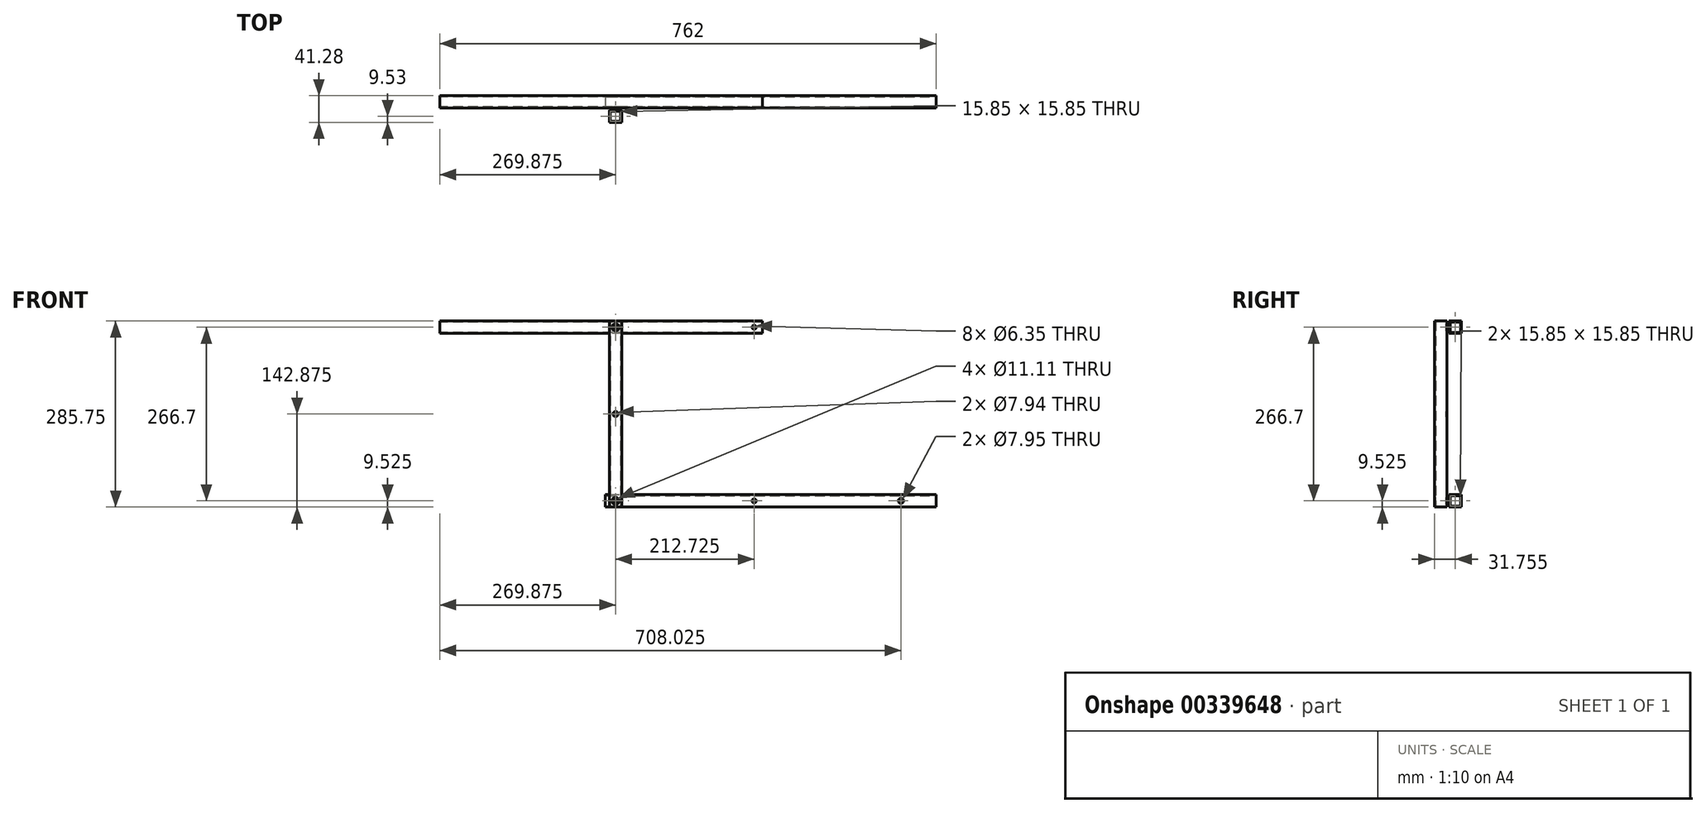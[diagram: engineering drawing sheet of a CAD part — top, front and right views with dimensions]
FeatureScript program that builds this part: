
annotation { "Feature Type Name" : "Feature", "Feature Type Description" : "" }
export const myFeature = defineFeature(function(context is Context, id is Id, definition is map)
    precondition{}
    {
        {
            var Q0;
            Q0=qCreatedBy(makeId("Front.planeOp"),FACE);
            var sketch = newSketch(context, id + "F0", { "sketchPlane" : qUnion([Q0])});
            skLineSegment(sketch, "E0.bottom", {"start": v(0, 0) * mm, "end": v(508, 0) * mm});
            skLineSegment(sketch, "E0.top", {"start": v(0, 19.05) * mm, "end": v(508, 19.05) * mm});
            skLineSegment(sketch, "E0.left", {"start": v(0, 0) * mm, "end": v(0, 19.05) * mm});
            skLineSegment(sketch, "E0.right", {"start": v(508, 0) * mm, "end": v(508, 19.05) * mm});
            skSolve(sketch);
        }
        {
            var Q0;
            Q0=makeQuery(id+"F0.imprint","IMPRINT",FACE,{"disambiguationData":[TD([[makeQuery(id+"F0.imprint","IMPRINT",EDGE,{"derivedFrom":sQuery(id+"F0.wireOp",EDGE,"E0.bottom")}),1.0]])]});
            extrude(context, id + "F1", {"entities" : qUnion([Q0]), "oppositeDirection" : true, "depth" : 19.05 * mm});
        }
        {
            var Q0;
            Q0=makeQuery(id+"F1.opExtrude","SWEPT_FACE",FACE,{"disambiguationData":[OSD([sQuery(id+"F0.wireOp",EDGE,"E0.right")])]});
            var Q1;
            Q1=makeQuery(id+"F1.opExtrude","SWEPT_FACE",FACE,{"disambiguationData":[OSD([sQuery(id+"F0.wireOp",EDGE,"E0.left")])]});
            shell(context, id + "F2", {"entities" : qUnion([Q0, Q1]), "thickness" : 1.6 * mm});
        }
        {
            var Q0;
            Q0=makeQuery(id+"F1.opExtrude","CAP_FACE",FACE,{"disambiguationData":[OSD([sQuery(id+"F0.wireOp",EDGE,"E0.bottom"),sQuery(id+"F0.wireOp",EDGE,"E0.top"),sQuery(id+"F0.wireOp",EDGE,"E0.left"),sQuery(id+"F0.wireOp",EDGE,"E0.right")])],"isStart":true});
            var sketch = newSketch(context, id + "F3", { "sketchPlane" : qUnion([Q0])});
            skCircle(sketch, "E1", {"center": v(15.88, 9.53) * mm, "radius": 3.18 * mm});
            skPoint(sketch, "E1.centerSnap0", {"position": v(0, 9.53) * mm});
            skCircle(sketch, "E2", {"center": v(228.6, 9.53) * mm, "radius": 3.18 * mm});
            skSolve(sketch);
        }
        {
            var Q0;
            Q0=makeQuery(id+"F3.imprint","IMPRINT",FACE,{"disambiguationData":[TD([[makeQuery(id+"F3.imprint","IMPRINT",EDGE,{"derivedFrom":sQuery(id+"F3.wireOp",EDGE,"E2")}),1.0]])]});
            var Q1;
            Q1=makeQuery(id+"F3.imprint","IMPRINT",FACE,{"disambiguationData":[TD([[makeQuery(id+"F3.imprint","IMPRINT",EDGE,{"derivedFrom":sQuery(id+"F3.wireOp",EDGE,"E1")}),1.0]])]});
            extrude(context, id + "F4", {"entities" : qUnion([Q0, Q1]), "operationType" : NewBodyOperationType.REMOVE, "endBound" : BoundingType.THROUGH_ALL, "oppositeDirection" : true, "depth" : 25.4 * mm});
        }
        {
            var Q0;
            Q0=makeQuery(id+"F1.opExtrude","CAP_FACE",FACE,{"disambiguationData":[OSD([sQuery(id+"F0.wireOp",EDGE,"E0.bottom"),sQuery(id+"F0.wireOp",EDGE,"E0.top"),sQuery(id+"F0.wireOp",EDGE,"E0.left"),sQuery(id+"F0.wireOp",EDGE,"E0.right")])],"isStart":true});
            var sketch = newSketch(context, id + "F5", { "sketchPlane" : qUnion([Q0])});
            skCircle(sketch, "E3.0", {"center": v(15.88, 9.53) * mm, "radius": 3.18 * mm});
            skCircle(sketch, "E4.0", {"center": v(228.6, 9.53) * mm, "radius": 3.18 * mm});
            skLineSegment(sketch, "E5.0", {"start": v(0, 19.05) * mm, "end": v(508, 19.05) * mm});
            skLineSegment(sketch, "E6", {"start": v(228.6, 9.53) * mm, "end": v(228.6, 276.23) * mm});
            skLineSegment(sketch, "E7", {"start": v(15.87, 9.53) * mm, "end": v(15.87, 276.23) * mm});
            skLineSegment(sketch, "E8", {"start": v(228.6, 276.23) * mm, "end": v(-241.3, 276.23) * mm});
            skLineSegment(sketch, "E9", {"start": v(15.88, 9.53) * mm, "end": v(454.03, 9.53) * mm});
            skLineSegment(sketch, "E10", {"start": v(454.03, 9.52) * mm, "end": v(15.87, 142.88) * mm});
            skLineSegment(sketch, "E11", {"start": v(15.87, 142.88) * mm, "end": v(15.87, 276.23) * mm});
            skLineSegment(sketch, "E12.top", {"start": v(219.07, 0) * mm, "end": v(238.12, 0) * mm});
            skLineSegment(sketch, "E12.left", {"start": v(219.07, 285.75) * mm, "end": v(219.07, 0) * mm});
            skLineSegment(sketch, "E12.right", {"start": v(238.12, 285.75) * mm, "end": v(238.12, 0) * mm});
            skPoint(sketch, "E12.middle", {"position": v(228.6, 142.88) * mm});
            skLineSegment(sketch, "E13.top", {"start": v(6.35, 0) * mm, "end": v(25.4, 0) * mm});
            skLineSegment(sketch, "E13.left", {"start": v(6.35, 285.75) * mm, "end": v(6.35, 0) * mm});
            skLineSegment(sketch, "E13.right", {"start": v(25.4, 285.75) * mm, "end": v(25.4, 0) * mm});
            skPoint(sketch, "E13.middle", {"position": v(15.87, 142.88) * mm});
            skLineSegment(sketch, "E14.bottom", {"start": v(241.3, 285.75) * mm, "end": v(-254, 285.75) * mm});
            skLineSegment(sketch, "E14.top", {"start": v(241.3, 266.7) * mm, "end": v(-254, 266.7) * mm});
            skLineSegment(sketch, "E14.left", {"start": v(241.3, 285.75) * mm, "end": v(241.3, 266.7) * mm});
            skLineSegment(sketch, "E14.right", {"start": v(-254, 285.75) * mm, "end": v(-254, 266.7) * mm});
            skPoint(sketch, "E14.middle", {"position": v(-6.35, 276.23) * mm});
            skLineSegment(sketch, "E15", {"start": v(6.35, 285.75) * mm, "end": v(25.4, 285.75) * mm});
            skLineSegment(sketch, "E16", {"start": v(219.07, 285.75) * mm, "end": v(238.12, 285.75) * mm});
            skSolve(sketch);
        }
        {
            var Q0;
            Q0=qCreatedBy(makeId("Front.planeOp"),FACE);
            cPlane(context, id + "F6", {"entities" : qUnion([Q0]), "cplaneType" : CPlaneType.OFFSET, "offset" : 3.17 * mm, "width" : 152.4 * mm, "height" : 152.4 * mm});
        }
        {
            var Q0;
            Q0=qCreatedBy(id+"F6.planeOp",FACE);
            var sketch = newSketch(context, id + "F7", { "sketchPlane" : qUnion([Q0])});
            skLineSegment(sketch, "E17.0", {"start": v(6.35, 285.75) * mm, "end": v(6.35, 0) * mm});
            skLineSegment(sketch, "E18.0", {"start": v(25.4, 285.75) * mm, "end": v(25.4, 0) * mm});
            skLineSegment(sketch, "E19.0", {"start": v(6.35, 0) * mm, "end": v(25.4, 0) * mm});
            skLineSegment(sketch, "E20.0.0", {"start": v(25.4, 276.23) * mm, "end": v(25.4, 285.75) * mm});
            skLineSegment(sketch, "E20.0.2", {"start": v(6.35, 288.93) * mm, "end": v(6.35, 276.23) * mm});
            skLineSegment(sketch, "E20.0.3", {"start": v(6.35, 276.23) * mm, "end": v(15.87, 276.23) * mm, "construction": true});
            skLineSegment(sketch, "E20.0.4", {"start": v(15.87, 276.23) * mm, "end": v(25.4, 276.23) * mm, "construction": true});
            skCircle(sketch, "E21", {"center": v(15.87, 276.23) * mm, "radius": 5.56 * mm});
            skLineSegment(sketch, "E22.0", {"start": v(15.88, 9.53) * mm, "end": v(454.03, 9.53) * mm, "construction": true});
            skCircle(sketch, "E23", {"center": v(15.88, 9.53) * mm, "radius": 5.56 * mm});
            skLineSegment(sketch, "E24", {"start": v(6.35, 285.75) * mm, "end": v(25.4, 285.75) * mm});
            skSolve(sketch);
        }
        {
            var Q0;
            Q0=makeQuery(id+"F7.imprint","IMPRINT",FACE,{"disambiguationData":[TD([[makeQuery(id+"F7.imprint","IMPRINT",EDGE,{"derivedFrom":sQuery(id+"F7.wireOp",EDGE,"E17.0")}),1.0]])]});
            extrude(context, id + "F8", {"entities" : qUnion([Q0]), "depth" : 19.05 * mm});
        }
        {
            var Q0;
            Q0=makeQuery(id+"F8.opExtrude","SWEPT_FACE",FACE,{"disambiguationData":[OSD([sQuery(id+"F7.wireOp",EDGE,"E20.0.1")])]});
            var Q1;
            Q1=makeQuery(id+"F8.opExtrude","SWEPT_FACE",FACE,{"disambiguationData":[OSD([sQuery(id+"F7.wireOp",EDGE,"E21")])]});
            var Q2;
            Q2=makeQuery(id+"F8.opExtrude","SWEPT_FACE",FACE,{"disambiguationData":[OSD([sQuery(id+"F7.wireOp",EDGE,"E19.0")])]});
            var Q3;
            Q3=makeQuery(id+"F8.opExtrude","SWEPT_FACE",FACE,{"disambiguationData":[OSD([sQuery(id+"F7.wireOp",EDGE,"E23")])]});
            var Q4;
            Q4=makeQuery(id+"F8.opExtrude","SWEPT_FACE",FACE,{"disambiguationData":[OSD([sQuery(id+"F7.wireOp",EDGE,"E24")])]});
            shell(context, id + "F9", {"entities" : qUnion([Q0, Q1, Q2, Q3, Q4]), "thickness" : 1.6 * mm});
        }
        {
            var Q0;
            Q0=qCreatedBy(makeId("Front.planeOp"),FACE);
            var sketch = newSketch(context, id + "F10", { "sketchPlane" : qUnion([Q0])});
            skLineSegment(sketch, "E25.0", {"start": v(241.3, 285.75) * mm, "end": v(-254, 285.75) * mm});
            skLineSegment(sketch, "E26.0", {"start": v(241.3, 266.7) * mm, "end": v(-254, 266.7) * mm});
            skLineSegment(sketch, "E27.0", {"start": v(-254, 285.75) * mm, "end": v(-254, 266.7) * mm});
            skLineSegment(sketch, "E28", {"start": v(241.3, 266.7) * mm, "end": v(241.3, 285.75) * mm});
            skPoint(sketch, "E29.0", {"position": v(228.6, 276.23) * mm});
            skPoint(sketch, "E30.0", {"position": v(15.87, 276.23) * mm});
            skCircle(sketch, "E31", {"center": v(15.87, 276.23) * mm, "radius": 3.18 * mm});
            skCircle(sketch, "E32", {"center": v(228.6, 276.23) * mm, "radius": 3.18 * mm});
            skSolve(sketch);
        }
        {
            var Q0;
            Q0 = qSketchRegion(id + "F10", true);
            extrude(context, id + "F11", {"entities" : qUnion([Q0]), "depth" : -19.05 * mm});
        }
        {
            var Q0;
            Q0=makeQuery(id+"F11.opExtrude","SWEPT_FACE",FACE,{"disambiguationData":[OSD([sQuery(id+"F10.wireOp",EDGE,"E27.0")])]});
            var Q1;
            Q1=makeQuery(id+"F11.opExtrude","SWEPT_FACE",FACE,{"disambiguationData":[OSD([sQuery(id+"F10.wireOp",EDGE,"E31")])]});
            var Q2;
            Q2=makeQuery(id+"F11.opExtrude","SWEPT_FACE",FACE,{"disambiguationData":[OSD([sQuery(id+"F10.wireOp",EDGE,"E28")])]});
            var Q3;
            Q3=makeQuery(id+"F11.opExtrude","SWEPT_FACE",FACE,{"disambiguationData":[OSD([sQuery(id+"F10.wireOp",EDGE,"E32")])]});
            shell(context, id + "F12", {"entities" : qUnion([Q0, Q1, Q2, Q3]), "thickness" : 1.6 * mm});
        }
        {
            var Q0;
            Q0=makeQuery(id+"F8.opExtrude","CAP_FACE",FACE,{"disambiguationData":[OSD([sQuery(id+"F7.wireOp",EDGE,"E17.0"),sQuery(id+"F7.wireOp",EDGE,"E18.0"),sQuery(id+"F7.wireOp",EDGE,"E19.0"),sQuery(id+"F7.wireOp",EDGE,"E20.0.0"),sQuery(id+"F7.wireOp",EDGE,"E20.0.1"),sQuery(id+"F7.wireOp",EDGE,"E20.0.2"),sQuery(id+"F7.wireOp",EDGE,"E21"),sQuery(id+"F7.wireOp",EDGE,"E23")])],"isStart":false});
            var sketch = newSketch(context, id + "F13", { "sketchPlane" : qUnion([Q0])});
            skPoint(sketch, "E33.0", {"position": v(15.87, 142.88) * mm});
            skCircle(sketch, "E34", {"center": v(15.87, 142.88) * mm, "radius": 3.97 * mm});
            skSolve(sketch);
        }
        {
            var Q0;
            Q0=makeQuery(id+"F13.imprint","IMPRINT",FACE,{"disambiguationData":[TD([[makeQuery(id+"F13.imprint","IMPRINT",EDGE,{"derivedFrom":sQuery(id+"F13.wireOp",EDGE,"E34")}),1.0]])]});
            var Q1;
            Q1=sQuery(id+"F13.wireOp",EDGE,"E34");
            extrude(context, id + "F14", {"entities" : qUnion([Q0]), "operationType" : NewBodyOperationType.REMOVE, "surfaceEntities" : qUnion([Q1]), "oppositeDirection" : true, "depth" : 25.4 * mm});
        }
        {
            var Q0;
            {var subQ9=makeQuery(id+"F1.opExtrude","CAP_EDGE",EDGE,{"disambiguationData":[OSD([sQuery(id+"F0.wireOp",EDGE,"E0.right")])],"isStart":true});Q0=makeQuery(id+"F5.imprint","IMPRINT",FACE,{"disambiguationData":[TD([[makeQuery(id+"F5.imprint","IMPRINT",EDGE,{"derivedFrom":subQ9}),1.0]])]});}
            var sketch = newSketch(context, id + "F15", { "sketchPlane" : qUnion([Q0])});
            skPoint(sketch, "E35.0", {"position": v(454.03, 9.52) * mm});
            skCircle(sketch, "E36", {"center": v(454.03, 9.52) * mm, "radius": 3.98 * mm});
            skSolve(sketch);
        }
        {
            var Q0;
            Q0 = qSketchRegion(id + "F15", true);
            var Q1;
            Q1=sQuery(id+"F15.wireOp",EDGE,"E36");
            extrude(context, id + "F16", {"entities" : qUnion([Q0]), "operationType" : NewBodyOperationType.REMOVE, "surfaceEntities" : qUnion([Q1]), "endBound" : BoundingType.THROUGH_ALL, "oppositeDirection" : true, "depth" : 25.4 * mm});
        }
    });
